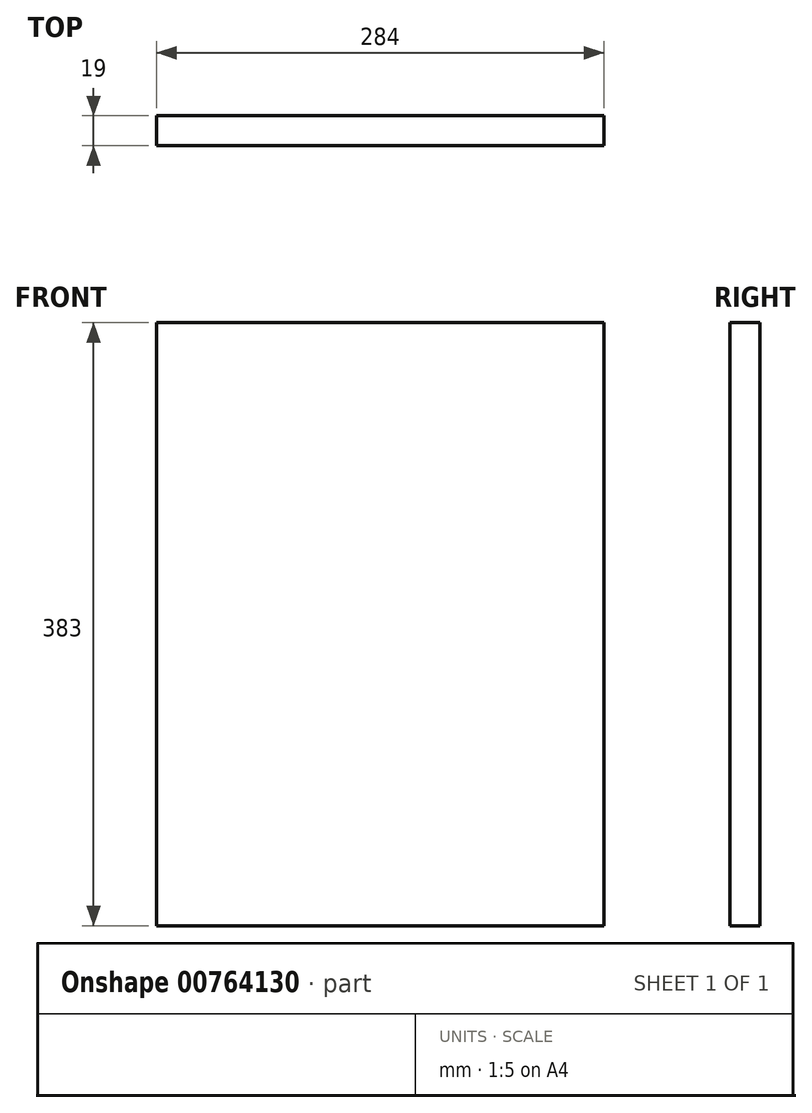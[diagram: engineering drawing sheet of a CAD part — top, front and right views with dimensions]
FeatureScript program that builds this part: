
annotation { "Feature Type Name" : "Feature", "Feature Type Description" : "" }
export const myFeature = defineFeature(function(context is Context, id is Id, definition is map)
    precondition{}
    {
        {
            var Q0;
            Q0=qCreatedBy(makeId("Front.planeOp"),FACE);
            var sketch = newSketch(context, id + "F0", { "sketchPlane" : qUnion([Q0])});
            skLineSegment(sketch, "E0.bottom", {"start": v(-130.2, 4.6) * mm, "end": v(153.8, 4.6) * mm});
            skLineSegment(sketch, "E0.top", {"start": v(-130.2, -378.4) * mm, "end": v(153.8, -378.4) * mm});
            skLineSegment(sketch, "E0.left", {"start": v(-130.2, 4.6) * mm, "end": v(-130.2, -378.4) * mm});
            skLineSegment(sketch, "E0.right", {"start": v(153.8, 4.6) * mm, "end": v(153.8, -378.4) * mm});
            skSolve(sketch);
        }
        {
            var Q0;
            Q0 = qSketchRegion(id + "F0", true);
            extrude(context, id + "F1", {"entities" : qUnion([Q0]), "depth" : 19 * mm, "offsetDistance" : 25 * mm});
        }
    });
